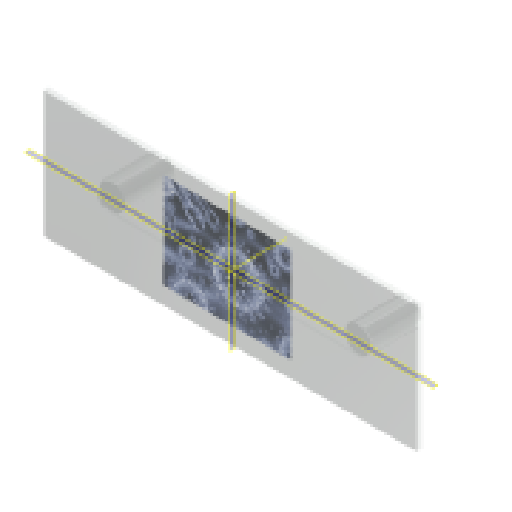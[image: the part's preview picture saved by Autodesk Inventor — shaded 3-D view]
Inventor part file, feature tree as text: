
AUTODESK INVENTOR PART (.ipt)
format: ipt  version: 2024.1 (Build 281209000, 209)  size: 4,368,384 bytes
history: native  units: mm
features: sketch x4, extrude x3, other x3, plane x2, projected_geometry x2
ambient origin geometry x8: Origin, YZ Plane, XZ Plane, XY Plane, X Axis, Y Axis, Z Axis, Center Point
bodies: Solid1 (feature_tree)
feature tree (14):
  extrude  "Extrusion1"  Depth=25.5mm
  other  "Decal1"
  other  "Arbeitsachse1"
  extrude  "Extrusion2"  Depth=25.0mm
  extrude  "Extrusion3"  Depth=0.5mm TaperAngle=0.0deg
  sketch  "Sketch1"  dims[d0=75.5mm d1=25.5mm]
  sketch  "Sketch2"  dims[d2=1.0mm d3=0.0mm d22=25.0mm]
  other  "Image2"
  plane  "Arbeitsebene1"
  plane  "Arbeitsebene2"
  sketch  "Skizze3"  dims[d23=5.0mm d24=0.5mm d25=0.0mm]
  projected_geometry  "Projizierte Kontur1"
  sketch  "Skizze4"  dims[d26=5.5mm d27=5.5mm d28=10.0mm d29=0.0mm]
  projected_geometry  "Projizierte Kontur2"
